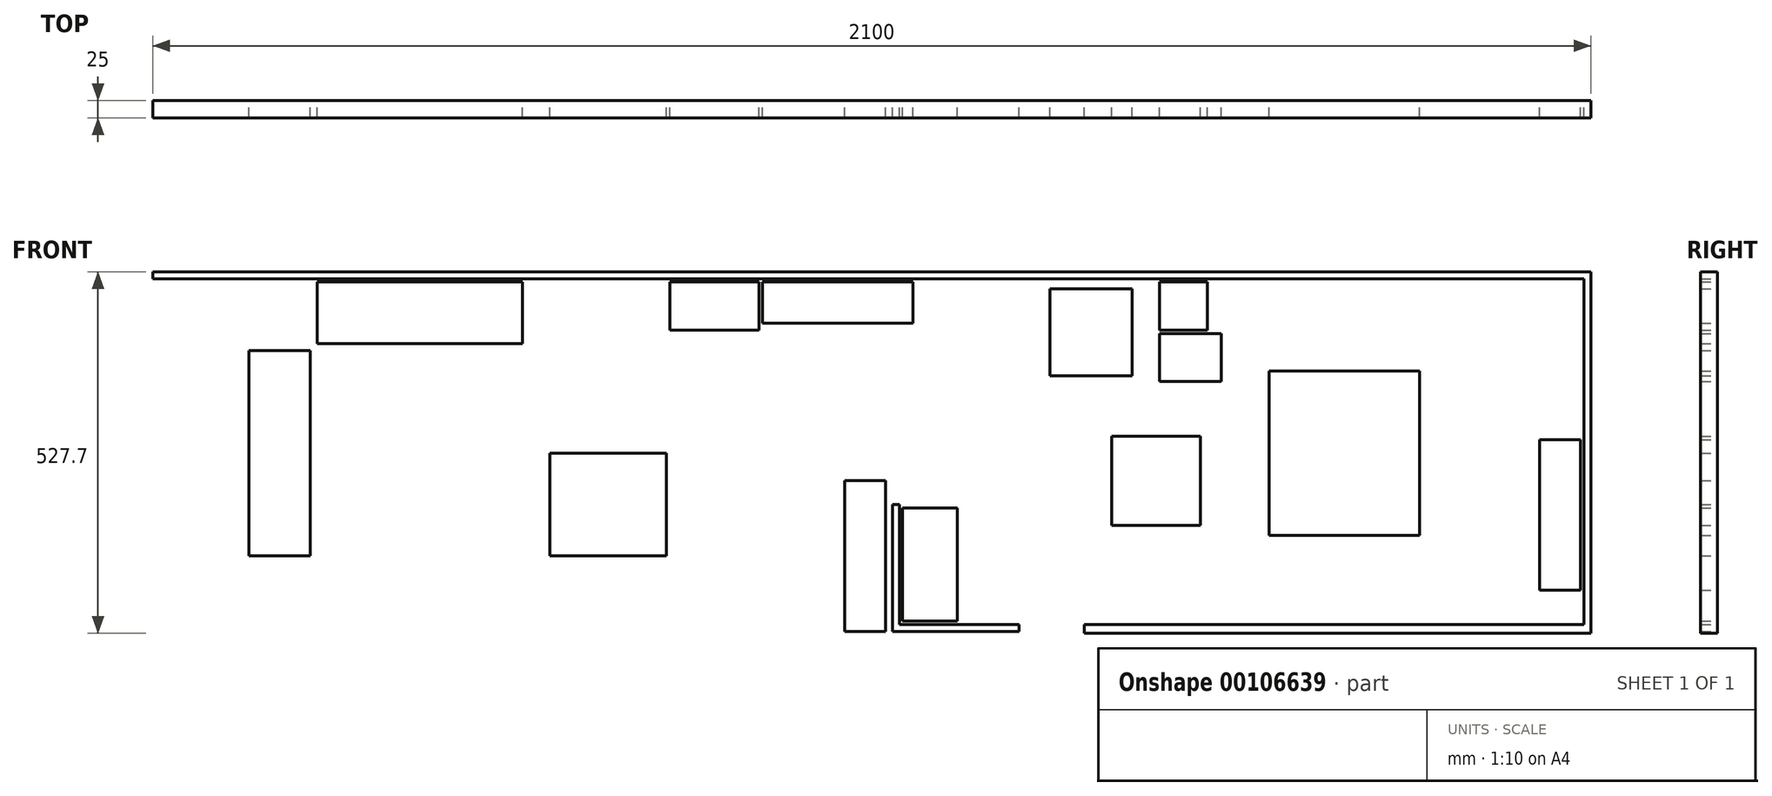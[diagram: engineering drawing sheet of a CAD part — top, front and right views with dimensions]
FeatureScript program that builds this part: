
annotation { "Feature Type Name" : "Feature", "Feature Type Description" : "" }
export const myFeature = defineFeature(function(context is Context, id is Id, definition is map)
    precondition{}
    {
        {
            var Q0;
            Q0=qCreatedBy(makeId("Front.planeOp"),FACE);
            var sketch = newSketch(context, id + "F0", { "sketchPlane" : qUnion([Q0])});
            skLineSegment(sketch, "E0.bottom", {"start": v(220, -120) * mm, "end": v(0, -120) * mm});
            skLineSegment(sketch, "E0.top", {"start": v(220, 120) * mm, "end": v(0, 120) * mm});
            skLineSegment(sketch, "E0.left", {"start": v(220, -120) * mm, "end": v(220, 120) * mm});
            skLineSegment(sketch, "E0.right", {"start": v(0, -120) * mm, "end": v(0, 120) * mm});
            skPoint(sketch, "E0.middle", {"position": v(110, 0) * mm});
            skLineSegment(sketch, "E1.bottom", {"start": v(470, 255) * mm, "end": v(-1630, 255) * mm});
            skLineSegment(sketch, "E1.top", {"start": v(470, 265) * mm, "end": v(-1630, 265) * mm});
            skLineSegment(sketch, "E1.left", {"start": v(470, 255) * mm, "end": v(470, 265) * mm});
            skLineSegment(sketch, "E1.right", {"start": v(-1630, 255) * mm, "end": v(-1630, 265) * mm});
            skLineSegment(sketch, "E2.bottom", {"start": v(-230, 25) * mm, "end": v(-100, 25) * mm});
            skLineSegment(sketch, "E2.top", {"start": v(-230, -105) * mm, "end": v(-100, -105) * mm});
            skLineSegment(sketch, "E2.left", {"start": v(-230, 25) * mm, "end": v(-230, -105) * mm});
            skLineSegment(sketch, "E2.right", {"start": v(-100, 25) * mm, "end": v(-100, -105) * mm});
            skLineSegment(sketch, "E3.bottom", {"start": v(-320, 240) * mm, "end": v(-200, 240) * mm});
            skLineSegment(sketch, "E3.top", {"start": v(-320, 113) * mm, "end": v(-200, 113) * mm});
            skLineSegment(sketch, "E3.left", {"start": v(-320, 240) * mm, "end": v(-320, 113) * mm});
            skLineSegment(sketch, "E3.right", {"start": v(-200, 240) * mm, "end": v(-200, 113) * mm});
            skLineSegment(sketch, "E4.bottom", {"start": v(-160, 175) * mm, "end": v(-70, 175) * mm});
            skLineSegment(sketch, "E4.top", {"start": v(-160, 105) * mm, "end": v(-70, 105) * mm});
            skLineSegment(sketch, "E4.left", {"start": v(-160, 175) * mm, "end": v(-160, 105) * mm});
            skLineSegment(sketch, "E4.right", {"start": v(-70, 175) * mm, "end": v(-70, 105) * mm});
            skLineSegment(sketch, "E5.bottom", {"start": v(-160, 250) * mm, "end": v(-90, 250) * mm});
            skLineSegment(sketch, "E5.top", {"start": v(-160, 180) * mm, "end": v(-90, 180) * mm});
            skLineSegment(sketch, "E5.left", {"start": v(-160, 250) * mm, "end": v(-160, 180) * mm});
            skLineSegment(sketch, "E5.right", {"start": v(-90, 250) * mm, "end": v(-90, 180) * mm});
            skLineSegment(sketch, "E6.bottom", {"start": v(-740, 250) * mm, "end": v(-520, 250) * mm});
            skLineSegment(sketch, "E6.top", {"start": v(-740, 190) * mm, "end": v(-520, 190) * mm});
            skLineSegment(sketch, "E6.left", {"start": v(-740, 250) * mm, "end": v(-740, 190) * mm});
            skLineSegment(sketch, "E6.right", {"start": v(-520, 250) * mm, "end": v(-520, 190) * mm});
            skLineSegment(sketch, "E7.bottom", {"start": v(-550, -75) * mm, "end": v(-540, -75) * mm});
            skLineSegment(sketch, "E7.top", {"start": v(-550, -260) * mm, "end": v(-540, -260) * mm});
            skLineSegment(sketch, "E7.left", {"start": v(-550, -75) * mm, "end": v(-550, -260) * mm});
            skLineSegment(sketch, "E7.right", {"start": v(-540, -75) * mm, "end": v(-540, -260) * mm});
            skLineSegment(sketch, "E8.bottom", {"start": v(-550, -260) * mm, "end": v(-365, -260) * mm});
            skLineSegment(sketch, "E8.top", {"start": v(-550, -250) * mm, "end": v(-365, -250) * mm});
            skLineSegment(sketch, "E8.left", {"start": v(-550, -260) * mm, "end": v(-550, -250) * mm});
            skLineSegment(sketch, "E8.right", {"start": v(-365, -260) * mm, "end": v(-365, -250) * mm});
            skLineSegment(sketch, "E9.bottom", {"start": v(-620, -40) * mm, "end": v(-560, -40) * mm});
            skLineSegment(sketch, "E9.top", {"start": v(-620, -260) * mm, "end": v(-560, -260) * mm});
            skLineSegment(sketch, "E9.left", {"start": v(-620, -40) * mm, "end": v(-620, -260) * mm});
            skLineSegment(sketch, "E9.right", {"start": v(-560, -40) * mm, "end": v(-560, -260) * mm});
            skLineSegment(sketch, "E10.bottom", {"start": v(-270, -250) * mm, "end": v(470, -250) * mm});
            skLineSegment(sketch, "E10.top", {"start": v(-270, -262.7) * mm, "end": v(470, -262.7) * mm});
            skLineSegment(sketch, "E10.left", {"start": v(-270, -250) * mm, "end": v(-270, -262.7) * mm});
            skLineSegment(sketch, "E10.right", {"start": v(470, -250) * mm, "end": v(470, -262.7) * mm});
            skLineSegment(sketch, "E11.bottom", {"start": v(-1050, 0) * mm, "end": v(-880, 0) * mm});
            skLineSegment(sketch, "E11.top", {"start": v(-1050, -150) * mm, "end": v(-880, -150) * mm});
            skLineSegment(sketch, "E11.left", {"start": v(-1050, 0) * mm, "end": v(-1050, -150) * mm});
            skLineSegment(sketch, "E11.right", {"start": v(-880, 0) * mm, "end": v(-880, -150) * mm});
            skLineSegment(sketch, "E12.bottom", {"start": v(-1390, 250) * mm, "end": v(-1090, 250) * mm});
            skLineSegment(sketch, "E12.top", {"start": v(-1390, 160) * mm, "end": v(-1090, 160) * mm});
            skLineSegment(sketch, "E12.left", {"start": v(-1390, 250) * mm, "end": v(-1390, 160) * mm});
            skLineSegment(sketch, "E12.right", {"start": v(-1090, 250) * mm, "end": v(-1090, 160) * mm});
            skLineSegment(sketch, "E13.bottom", {"start": v(-1490, 150) * mm, "end": v(-1400, 150) * mm});
            skLineSegment(sketch, "E13.top", {"start": v(-1490, -150) * mm, "end": v(-1400, -150) * mm});
            skLineSegment(sketch, "E13.left", {"start": v(-1490, 150) * mm, "end": v(-1490, -150) * mm});
            skLineSegment(sketch, "E13.right", {"start": v(-1400, 150) * mm, "end": v(-1400, -150) * mm});
            skLineSegment(sketch, "E14.bottom", {"start": v(-535, -245) * mm, "end": v(-455, -245) * mm});
            skLineSegment(sketch, "E14.top", {"start": v(-535, -80) * mm, "end": v(-455, -80) * mm});
            skLineSegment(sketch, "E14.left", {"start": v(-535, -245) * mm, "end": v(-535, -80) * mm});
            skLineSegment(sketch, "E14.right", {"start": v(-455, -245) * mm, "end": v(-455, -80) * mm});
            skLineSegment(sketch, "E15.bottom", {"start": v(-875, 250) * mm, "end": v(-745, 250) * mm});
            skLineSegment(sketch, "E15.top", {"start": v(-875, 180) * mm, "end": v(-745, 180) * mm});
            skLineSegment(sketch, "E15.left", {"start": v(-875, 250) * mm, "end": v(-875, 180) * mm});
            skLineSegment(sketch, "E15.right", {"start": v(-745, 250) * mm, "end": v(-745, 180) * mm});
            skLineSegment(sketch, "E16.bottom", {"start": v(470, 265) * mm, "end": v(460, 265) * mm});
            skLineSegment(sketch, "E16.top", {"start": v(470, -262.7) * mm, "end": v(460, -262.7) * mm});
            skLineSegment(sketch, "E16.left", {"start": v(470, 265) * mm, "end": v(470, -262.7) * mm});
            skLineSegment(sketch, "E16.right", {"start": v(460, 265) * mm, "end": v(460, -262.7) * mm});
            skLineSegment(sketch, "E17.bottom", {"start": v(395, 20) * mm, "end": v(455, 20) * mm});
            skLineSegment(sketch, "E17.top", {"start": v(395, -200) * mm, "end": v(455, -200) * mm});
            skLineSegment(sketch, "E17.left", {"start": v(395, 20) * mm, "end": v(395, -200) * mm});
            skLineSegment(sketch, "E17.right", {"start": v(455, 20) * mm, "end": v(455, -200) * mm});
            skSolve(sketch);
        }
        {
            var Q0;
            Q0 = qSketchRegion(id + "F0", true);
            extrude(context, id + "F1", {"entities" : qUnion([Q0]), "depth" : 25 * mm});
        }
    });
